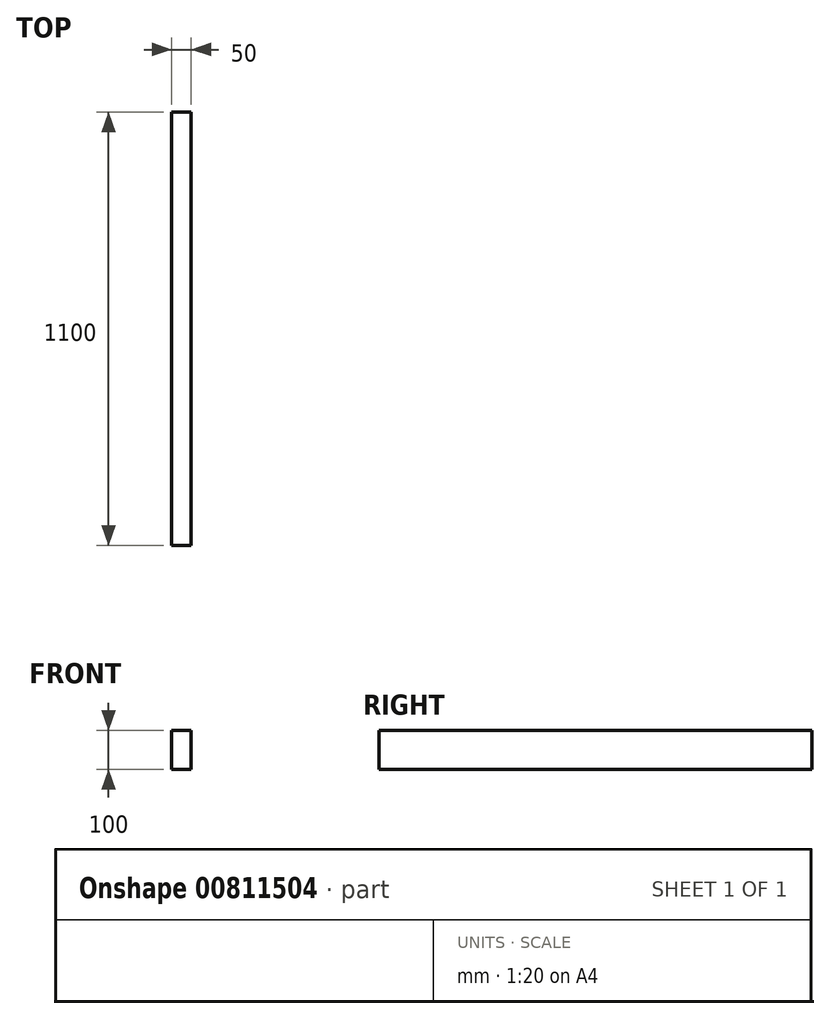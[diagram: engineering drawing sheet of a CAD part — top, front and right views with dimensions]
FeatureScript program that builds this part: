
annotation { "Feature Type Name" : "Feature", "Feature Type Description" : "" }
export const myFeature = defineFeature(function(context is Context, id is Id, definition is map)
    precondition{}
    {
        {
            var Q0;
            Q0=qCreatedBy(makeId("Front.planeOp"),FACE);
            var sketch = newSketch(context, id + "F0", { "sketchPlane" : qUnion([Q0])});
            skLineSegment(sketch, "E0.bottom", {"start": v(25, 50) * mm, "end": v(-25, 50) * mm});
            skLineSegment(sketch, "E0.top", {"start": v(25, -50) * mm, "end": v(-25, -50) * mm});
            skLineSegment(sketch, "E0.left", {"start": v(25, 50) * mm, "end": v(25, -50) * mm});
            skLineSegment(sketch, "E0.right", {"start": v(-25, 50) * mm, "end": v(-25, -50) * mm});
            skPoint(sketch, "E0.middle", {"position": v(0, 0) * mm});
            skSolve(sketch);
        }
        {
            var Q0;
            Q0=makeQuery(id+"F0.imprint","IMPRINT",FACE,{"disambiguationData":[TD([[makeQuery(id+"F0.imprint","IMPRINT",EDGE,{"derivedFrom":sQuery(id+"F0.wireOp",EDGE,"E0.bottom")}),1.0]])]});
            extrude(context, id + "F1", {"entities" : qUnion([Q0]), "endBound" : BoundingType.SYMMETRIC, "depth" : 1100 * mm, "offsetDistance" : 25.4 * mm});
        }
    });
